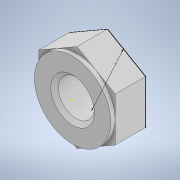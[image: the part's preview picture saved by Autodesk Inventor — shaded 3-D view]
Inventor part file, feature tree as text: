
AUTODESK INVENTOR PART (.ipt)
format: ipt  version: 2020 (Build 240168000, 168)  size: 146,944 bytes
history: native  units: mm
features: sketch x7, extrude x3, chamfer x2, other x1
ambient origin geometry x8: Origin, YZ Plane, XZ Plane, XY Plane, X Axis, Y Axis, Z Axis, Center Point
bodies: Body1 (feature_tree)
feature tree (13):
  other  "Bryła1"
  extrude  "Wyciągnięcie proste1"  Depth=7.0mm
  chamfer  "Faza1"  Distance=3.3mm
  sketch  "Szkic2"
  extrude  "Wyciągnięcie proste2"  Depth=0.4mm TaperAngle=0.0deg
  extrude  "Wyciągnięcie proste3"  Depth=0.35mm TaperAngle=45.0deg
  chamfer  "Faza2"  Distance=2.8mm
  sketch  "Szkic5"
  sketch  "Szkic6"
  sketch  "Szkic7"
  sketch  "Szkic1"
  sketch  "Szkic3"
  sketch  "Szkic4"
